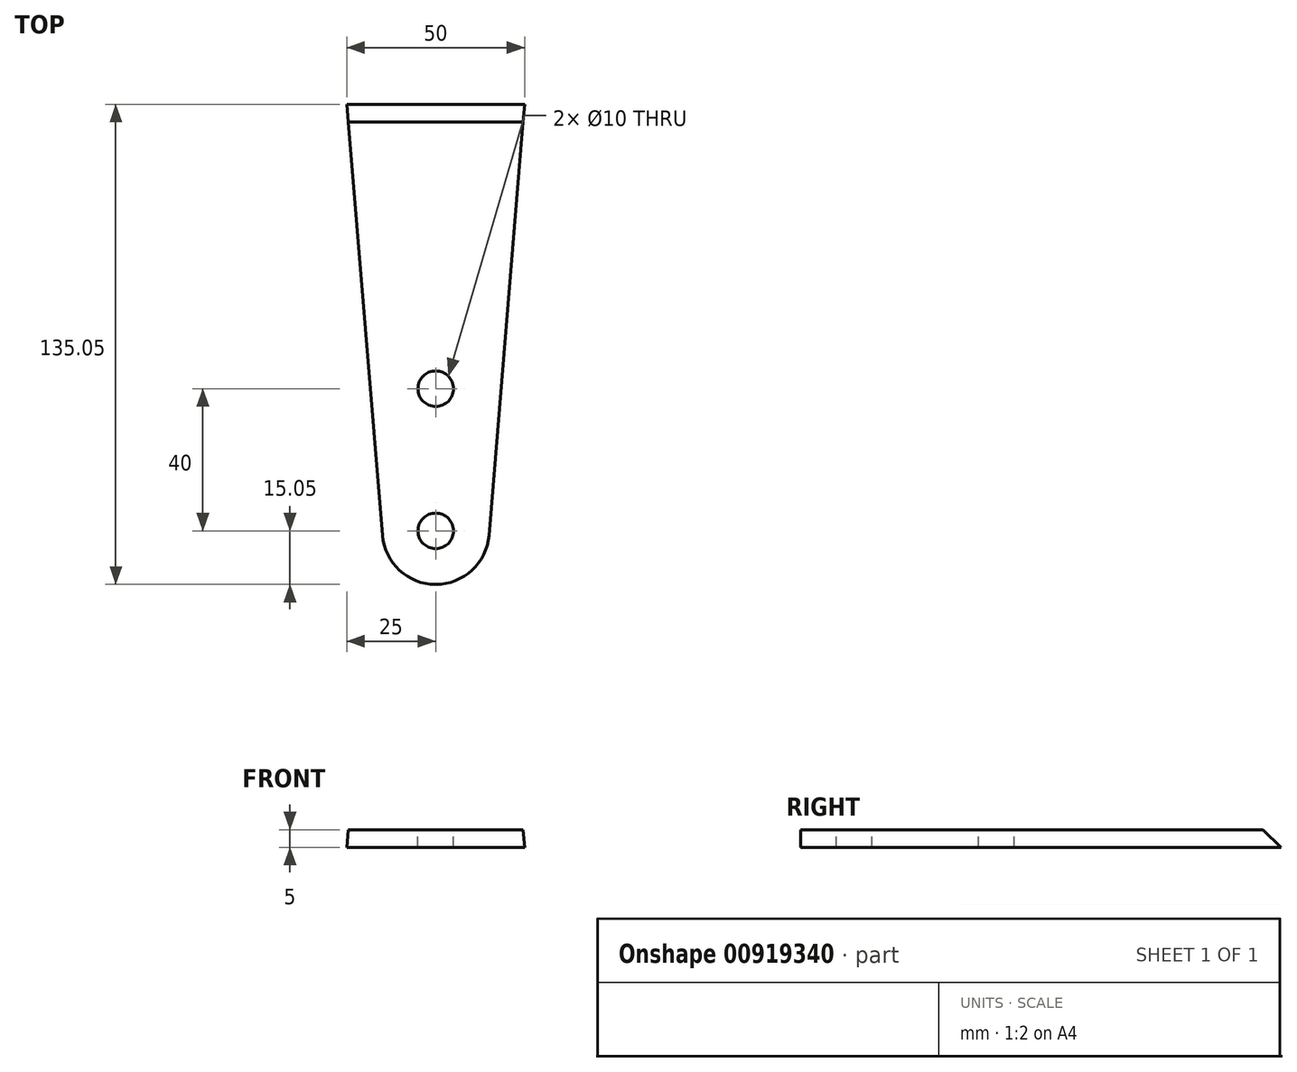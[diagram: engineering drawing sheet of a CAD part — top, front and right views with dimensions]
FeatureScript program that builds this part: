
annotation { "Feature Type Name" : "Feature", "Feature Type Description" : "" }
export const myFeature = defineFeature(function(context is Context, id is Id, definition is map)
    precondition{}
    {
        {
            var Q0;
            Q0=qCreatedBy(makeId("Top.planeOp"),FACE);
            var sketch = newSketch(context, id + "F0", { "sketchPlane" : qUnion([Q0])});
            skLineSegment(sketch, "E0", {"start": v(0, 0) * mm, "end": v(50, 0) * mm});
            skLineSegment(sketch, "E1", {"start": v(50, 0) * mm, "end": v(40, -121.24) * mm});
            skArc(sketch, "E2", {"start": v(40, -121.24) * mm, "mid": v(25, -135.05) * mm, "end": v(10, -121.24) * mm});
            skLineSegment(sketch, "E3", {"start": v(10, -121.24) * mm, "end": v(0, 0) * mm});
            skSolve(sketch);
        }
        {
            var Q0;
            Q0=makeQuery(id+"F0.imprint","IMPRINT",FACE,{"disambiguationData":[TD([[makeQuery(id+"F0.imprint","IMPRINT",EDGE,{"derivedFrom":sQuery(id+"F0.wireOp",EDGE,"E0")}),-1.0]])]});
            extrude(context, id + "F1", {"entities" : qUnion([Q0]), "depth" : 5 * mm, "offsetDistance" : 25 * mm});
        }
        {
            var Q0;
            Q0=qCreatedBy(makeId("Right.planeOp"),FACE);
            var sketch = newSketch(context, id + "F2", { "sketchPlane" : qUnion([Q0])});
            skLineSegment(sketch, "E4", {"start": v(0, 0) * mm, "end": v(-5, 5) * mm});
            skLineSegment(sketch, "E5", {"start": v(-5, 5) * mm, "end": v(0, 5) * mm});
            skLineSegment(sketch, "E6", {"start": v(0, 5) * mm, "end": v(0, 0) * mm});
            skSolve(sketch);
        }
        {
            var Q0;
            Q0 = qSketchRegion(id + "F2", true);
            extrude(context, id + "F3", {"entities" : qUnion([Q0]), "operationType" : NewBodyOperationType.REMOVE, "endBound" : BoundingType.THROUGH_ALL, "depth" : 25 * mm, "offsetDistance" : 25 * mm});
        }
        {
            var Q0;
            Q0=makeQuery(id+"F1.opExtrude","CAP_FACE",FACE,{"disambiguationData":[OSD([sQuery(id+"F0.wireOp",EDGE,"E0"),sQuery(id+"F0.wireOp",EDGE,"E1"),sQuery(id+"F0.wireOp",EDGE,"E2"),sQuery(id+"F0.wireOp",EDGE,"E3")])],"isStart":false});
            var sketch = newSketch(context, id + "F4", { "sketchPlane" : qUnion([Q0])});
            skPoint(sketch, "E7", {"position": v(25, -120) * mm});
            skPoint(sketch, "E8", {"position": v(25, -80) * mm});
            skSolve(sketch);
        }
        {
            var Q0;
            Q0=sQuery(id+"F4.wireOp",VERTEX,"E7");
            var Q1;
            Q1=sQuery(id+"F4.wireOp",VERTEX,"E8");
            var Q2;
            Q2=makeQuery(id+"F1.opExtrude","SWEPT_BODY",BODY,{"disambiguationData":[OSD([sQuery(id+"F0.wireOp",EDGE,"E0"),sQuery(id+"F0.wireOp",EDGE,"E1"),sQuery(id+"F0.wireOp",EDGE,"E2"),sQuery(id+"F0.wireOp",EDGE,"E3")])]});
            hole(context, id + "F5", {"style" : HoleStyle.SIMPLE, "endStyle" : HoleEndStyle.BLIND, "holeDiameter" : 10 * mm, "majorDiameter" : 5 * mm, "holeDepth" : 100 * mm, "isTappedThrough" : true, "tappedDepth" : 12 * mm, "tapClearance" : 3, "locations" : qUnion([Q0, Q1]), "scope" : qUnion([Q2])});
        }
    });
